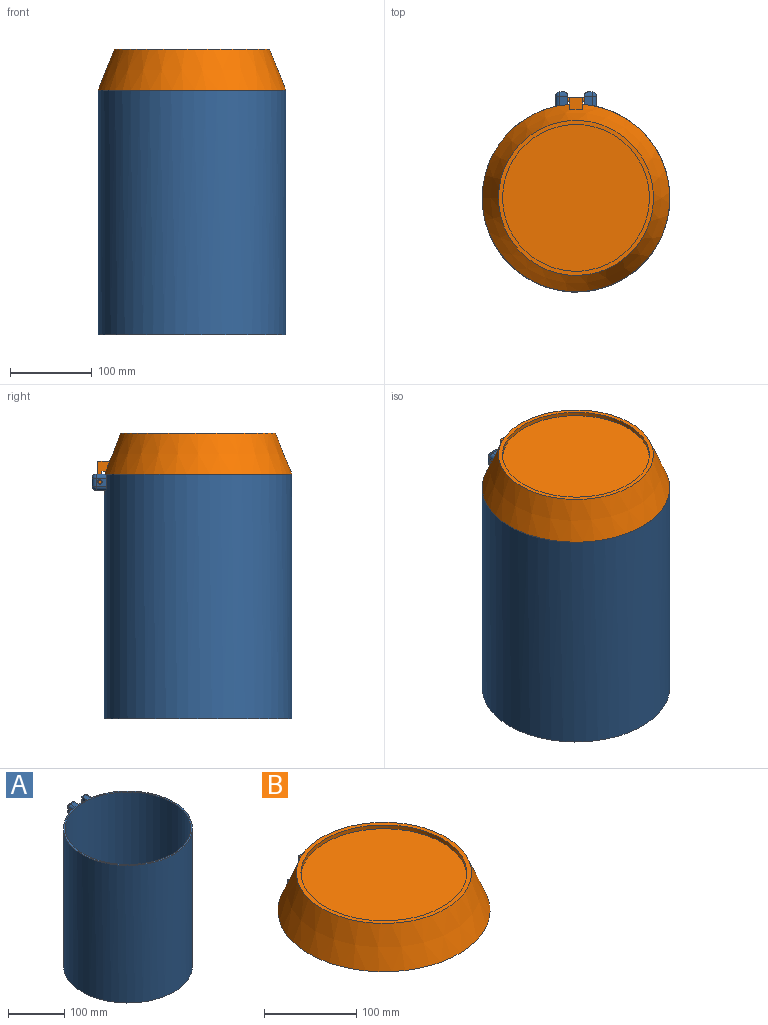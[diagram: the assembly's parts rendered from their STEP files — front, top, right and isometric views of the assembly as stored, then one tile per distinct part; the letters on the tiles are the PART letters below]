
ASSEMBLY  parts=2 mates=1
PART A: 34 faces, bbox 230x245x300 mm
  f0: plane 239.92x230mm, normal (0,0,1), area 2339.3mm2, adj f1,f2,f6,f13,f14,f15,f17,f22
  f1: cylinder r=115mm len=300mm, axis (0,0,-1), area 215670.7mm2, adj f0,f2,f3,f5,f8,f9,f10,f12
  f2: cylinder r=115mm len=5.08mm, axis (0,0,-1), area 5.7mm2, adj f0,f1,f17
  f3: plane 11.66x9.92mm, normal (0,0,-1), area 108.5mm2, adj f1,f13,f16,f21
  f4: plane 9.84x4.84mm, normal (0,1,0), area 47.6mm2, adj f18,f21,f22,f23
  f5: plane 230x230mm, normal (0,0,-1), area 41547.6mm2, adj f1
  f6: cylinder r=112mm len=297mm, axis (0,0,-1), area 209003.9mm2, adj f0,f7
  f7: plane 224x224mm, normal (0,0,1), area 39408.1mm2, adj f6
  f8: plane 12.67x9.84mm, normal (-1,0,0), area 101.2mm2, adj f1,f16,f17,f18,f33
  f9: plane 12.67x9.84mm, normal (1,0,0), area 101.2mm2, adj f1,f24,f25,f26,f32
  f10: plane 11.66x9.92mm, normal (0,0,-1), area 108.5mm2, adj f1,f14,f24,f29
  f11: plane 9.84x4.84mm, normal (0,1,0), area 47.6mm2, adj f25,f29,f30,f31
  f12: plane 20x1mm, normal (0,0,1), area 17.1mm2, adj f1,f13,f14,f15
  f13: plane 25.4x10.92mm, normal (1,0,0), area 198mm2, adj f0,f1,f3,f12,f15,f23,f33
  f14: plane 25.4x10.92mm, normal (-1,0,0), area 198mm2, adj f0,f1,f10,f12,f15,f31,f32
  f15: plane 25.4x20mm, normal (0,1,0), area 508mm2, adj f0,f12,f13,f14
  f16: cylinder r=5.08mm len=12.67mm, axis (0,-1,0), area 98mm2, adj f1,f3,f8,f19
  f17: cylinder r=5.08mm len=12.67mm, axis (0,-1,0), area 98mm2, adj f0,f2,f8,f20
  f18: cylinder r=5.08mm len=9.84mm, axis (0,0,1), area 78.5mm2, adj f4,f8,f19,f20
  f19: sphere r=5.08mm, area 40.5mm2, adj f16,f18,f21
  f20: sphere r=5.08mm, area 40.5mm2, adj f17,f18,f22
  f21: cylinder r=5.08mm len=9.92mm, axis (-1,0,0), area 64.4mm2, adj f3,f4,f19,f23
  f22: cylinder r=5.08mm len=9.92mm, axis (-1,0,0), area 64.4mm2, adj f0,f4,f20,f23
  f23: cylinder r=5.08mm len=20mm, axis (0,0,-1), area 130.1mm2, adj f4,f13,f21,f22
  f24: cylinder r=5.08mm len=12.67mm, axis (0,1,0), area 98mm2, adj f1,f9,f10,f27
  f25: cylinder r=5.08mm len=9.84mm, axis (0,0,-1), area 78.5mm2, adj f9,f11,f27,f28
  f26: cylinder r=5.08mm len=12.67mm, axis (0,1,0), area 98mm2, adj f0,f1,f9,f28
  f27: sphere r=5.08mm, area 40.5mm2, adj f24,f25,f29
  f28: sphere r=5.08mm, area 40.5mm2, adj f25,f26,f30
  f29: cylinder r=5.08mm len=9.92mm, axis (-1,0,0), area 64.4mm2, adj f10,f11,f27,f31
  f30: cylinder r=5.08mm len=9.92mm, axis (-1,0,0), area 64.4mm2, adj f0,f11,f28,f31
  f31: cylinder r=5.08mm len=20mm, axis (0,0,1), area 130.1mm2, adj f11,f14,f29,f30
  f32: cylinder r=2.73mm len=15mm, axis (1,0,0), area 257.6mm2, adj f9,f14
  f33: cylinder r=2.73mm len=15mm, axis (1,0,0), area 257.6mm2, adj f8,f13
PART B: 18 faces, bbox 230x238.1x62.1 mm
  f0: cone r=115mm half-angle=21.8deg, axis (0,0,-1), area 35308.3mm2, adj f1,f2,f12,f14,f15,f17
  f1: plane 190x190mm, normal (0,0,1), area 2906mm2, adj f0,f3
  f2: plane 230x230mm, normal (0,0,-1), area 2301.9mm2, adj f0,f5
  f3: cylinder r=90mm len=180mm, axis (0,0,1), area 2827.4mm2, adj f1,f4
  f4: plane 180x180mm, normal (0,0,1), area 25446.9mm2, adj f3
  f5: cone r=112.21mm half-angle=21.8deg, axis (0,0,-1), area 32510.4mm2, adj f2,f6
  f6: cylinder r=93mm len=186mm, axis (0,0,1), area 2876.3mm2, adj f5,f7
  f7: plane 186x186mm, normal (0,0,-1), area 27171.6mm2, adj f6
  f8: plane 17x11.97mm, normal (0,-1,0), area 203.5mm2, adj f9,f12,f14,f17
  f9: cylinder r=2.5mm len=50mm, axis (1,0,0), area 663.1mm2, adj f8,f10,f11,f12,f14,f16
  f10: plane 5x5mm, normal (-1,0,0), area 19.6mm2, adj f9
  f11: plane 5x5mm, normal (1,0,0), area 19.6mm2, adj f9
  f12: plane 25.41x14.63mm, normal (-1,0,0), area 201.8mm2, adj f0,f8,f9,f13,f15,f16,f17
  f13: plane 25.4x17mm, normal (0,1,0), area 431.8mm2, adj f12,f14,f15,f16
  f14: plane 25.41x14.63mm, normal (1,0,0), area 201.8mm2, adj f0,f8,f9,f13,f15,f16,f17
  f15: plane 17x14.62mm, normal (0,0,1), area 244.8mm2, adj f0,f12,f13,f14
  f16: plane 17x0.26mm, normal (0,0,-1), area 4.5mm2, adj f9,f12,f13,f14
  f17: plane 17x4.82mm, normal (0,0,-1), area 78.3mm2, adj f0,f8,f12,f14
PLACE A at identity
PLACE B at identity
MATE revolute A.f32 <-> B.f9  axis (1,0,0) through (25,120.4,290.41)mm
